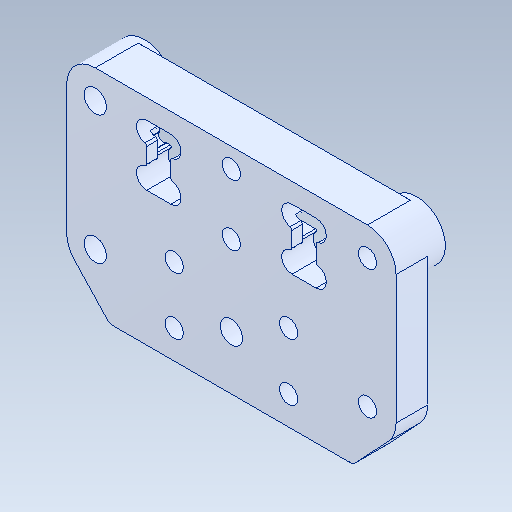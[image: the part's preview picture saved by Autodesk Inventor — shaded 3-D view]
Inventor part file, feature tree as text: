
AUTODESK INVENTOR PART (.ipt)
format: ipt  version: 2020 (Build 240168000, 168)  size: 221,696 bytes
history: native  units: in
note: dims shown in document units (in); Inventor stores cm internally (conversion verified against a paired STEP export)
features: fillet x1
ambient origin geometry x8: Origin, YZ Plane, XZ Plane, XY Plane, X Axis, Y Axis, Z Axis, Center Point
bodies: Solid1 (feature_tree)
feature tree (1):
  fillet  "Fillet10"  [1 undecoded]
note: 1 required parameter value undecoded (feature->parameter linkage not recoverable at this tier; creation-order binding heuristic only, values carry confidence <= 0.55)
